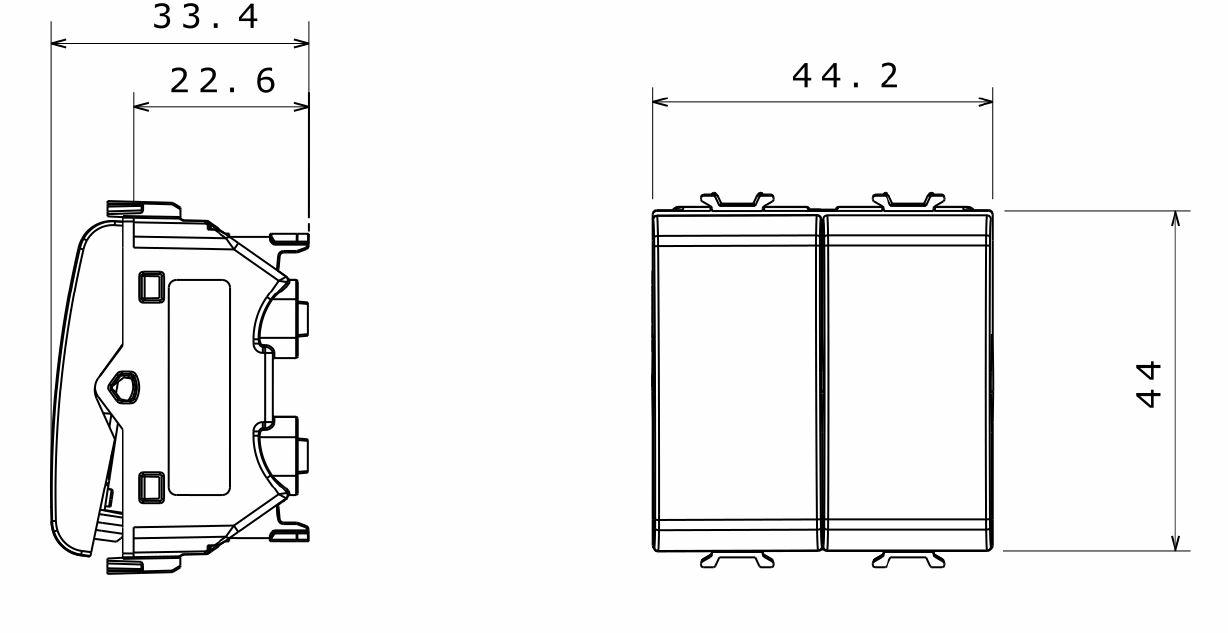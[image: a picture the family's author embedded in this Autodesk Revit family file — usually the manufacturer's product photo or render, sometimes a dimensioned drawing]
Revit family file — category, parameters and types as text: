
# Revit family: Domotics-DomesticRanges-GEWISS-CHORUS_COMMAND-PUSH-BUTTON_ELECTRONIC_1M
name_source: partatom
category: Apparecchi elettrici
revit_build: Autodesk Revit 2016 (Build: 20161004_0715(x64)
units: mm (PartAtom-declared; Revit-internal decimal feet)

## family parameters
Condiviso = Sì
Host = Superficie
Mantenere orientamento annotazione = Sì
Punto di calcolo locali = Sì
Quota connettore circolare = Usa diametro
Taglio con vuoti quando caricato = Sì
Tipo di parte = Normale

## types (15) — shared parameters
12 = No
13 = No
14 = No
15 = No
16 = Sì
Catalogue = DOMOTICS
Catalogue Range = CHORUS - DOMESTIC RANGE
Description. = Electronic push-button
IDF = 69217882-810e-4cb6-b3cc-5f85b68fef88
IDT = 900c6326-e09f-4f61-a302-cdb04b636b19
Immagine tipo = GW14916.jpg
N. moduli Chorus = 1
No. Chorus modules: = 1
Produttore = GEWISS S.p.A.
Prospetto di default = 1219 mm
SEO = Push button
Technical sheet = https://www.gewiss.com
Tipo pulsante = CHORUS PULSANTI ELETTRONICI 1M_GENERICO : GW14916 Pulsante elettronico 1M segnalazione luminosa titanio
Tipo simbolo = PULSANTI : LUM
URL = https://www.gewiss.com
Version file RFA = 19.0
tipo pulsante = 5

## per-type parameters (varying)
| type | Button key | Colore | Descrizione | EAN code | Electrocod | GW - Ingressi | GW - Tensione di alimentazione | GW - Tipo di contatto | GW - Tipo di impiego | Modello | Tipo | Type of use: | Type: |
| GW14913 - Backlit electronic bus push-button 1M titanium | With diffuser | Titanium | BACKLIT ELECTRONIC BUS PUSH-BUTTON 1M T | 8011564705135 | 0141 | BUS |  | Potential-free | Bus contacts interfaces | GW14913 | Backlit | Bus contacts interfaces | Backlit |
| GW14915 - Universal electronic push-button 1M titanium | Neutral | Titanium | UNIVERSAL ELECTRONIC PUSH-BUTTON 1M T | 8011564764149 | 0141 |  |  | Potential-free | Relay, dimmer, bus contacts interfaces | GW14915 | General | Relay, dimmer, bus contacts interfaces |  |
| GW10915 - Universal electronic push-button 1M white | Neutral | White | UNIVERSAL ELECTRONIC PUSH-BUTTON 1M W | 8011564764125 | 0141 |  |  | Potential-free | Relay, dimmer, bus contacts interfaces | GW10915 | General | Relay, dimmer, bus contacts interfaces |  |
| GW10912 - Backlit electronic push-button 1M white | With diffuser | White | BACKLIT ELECTRONIC PUSH-BUTTON 1M W | 8011564705050 | 0141 |  | 230 V ac - 50/60 Hz |  | Relay, dimmer | GW10912 | Backlit | Relay, dimmer | Backlit |
| GW14916 - Electronic push-button 1M indicator titanium | With replaceable neutral lens | Titanium | ELECTRONIC PUSH-BUTTON 1M INDICATOR TI. | 8011564816473 | 0144 | BUS |  | Potential-free | Bus contacts interfaces | GW14916 | Indicator |  | Backlit |
| GW10913 - Backlit electronic bus push-button 1M white | With diffuser | White | BACKLIT ELECTRONIC BUS PUSH-BUTTON 1M W | 8011564705067 | 0141 | BUS |  | Potential-free | Bus contacts interfaces | GW10913 | Backlit | Bus contacts interfaces | Backlit |
| GW10914 - Double electronic push-button 1M white | Neutral | White | DOUBLE ELECTRONIC PUSH-BUTTON 1M W | 8011564705074 | 0141 |  |  | Dual, potential-free and with interlock | Roller shutters | GW10914 | UP - DOWN arrow | Roller shutters |  |
| GW12916 - Electronic push-button 1M indicator black | With replaceable neutral lens | Black | ELECTRONIC PUSH-BUTTON 1M INDICATOR BL. | 8011564816442 | 0144 | BUS |  | Potential-free | Bus contacts interfaces | GW12916 | Indicator |  | Backlit |
| GW14914 - Double electronic push-button 1M titanium | Neutral | Titanium | DOUBLE ELECTRONIC PUSH-BUTTON 1M T | 8011564705142 | 0141 |  |  | Dual, potential-free and with interlock | Roller shutters | GW14914 | UP - DOWN arrow | Roller shutters |  |
| GW12913 - Backlit electronic bus push-button 1M black | With diffuser | Black | BACKLIT ELECTRONIC BUS PUSH-BUTTON 1M B | 8011564705098 | 0141 | BUS |  | Potential-free | Bus contacts interfaces | GW12913 | Backlit | Bus contacts interfaces | Backlit |
| GW14912 - Backlit electronic push-button 1M titanium | With diffuser | Titanium | BACKLIT ELECTRONIC PUSH-BUTTON 1M T | 8011564705128 | 0141 |  | 230 V ac - 50/60 Hz |  | Relay, dimmer | GW14912 | Backlit | Relay, dimmer | Backlit |
| GW12915 - Universal electronic push-button 1M black | Neutral | Black | UNIVERSAL ELECTRONIC PUSH-BUTTON 1M B | 8011564764132 | 0141 |  |  | Potential-free | Relay, dimmer, bus contacts interfaces | GW12915 | General | Relay, dimmer, bus contacts interfaces |  |
| GW12912 - Backlit electronic push-button 1M black | With diffuser | Black | BACKLIT ELECTRONIC PUSH-BUTTON 1M B | 8011564705081 | 0141 |  | 230 V ac - 50/60 Hz |  | Relay, dimmer | GW12912 | Backlit | Relay, dimmer | Backlit |
| GW12914 - Double electronic push-button 1M black | Neutral | Black | DOUBLE ELECTRONIC PUSH-BUTTON 1M B | 8011564705104 | 0141 |  |  | Dual, potential-free and with interlock | Roller shutters | GW12914 | UP - DOWN arrow | Roller shutters |  |
| GW10916 - Electronic push-button 1M indicator white | With replaceable neutral lens | White | ELECTRONIC PUSH-BUTTON 1M INDICATOR WH | 8011564816411 | 0144 | BUS |  | Potential-free | Bus contacts interfaces | GW10916 | Indicator | Bus contacts interfaces | Backlit |

## geometry (parser evidence)
native form markers: Sweep x2
no freeform markers — native parametric forms only
